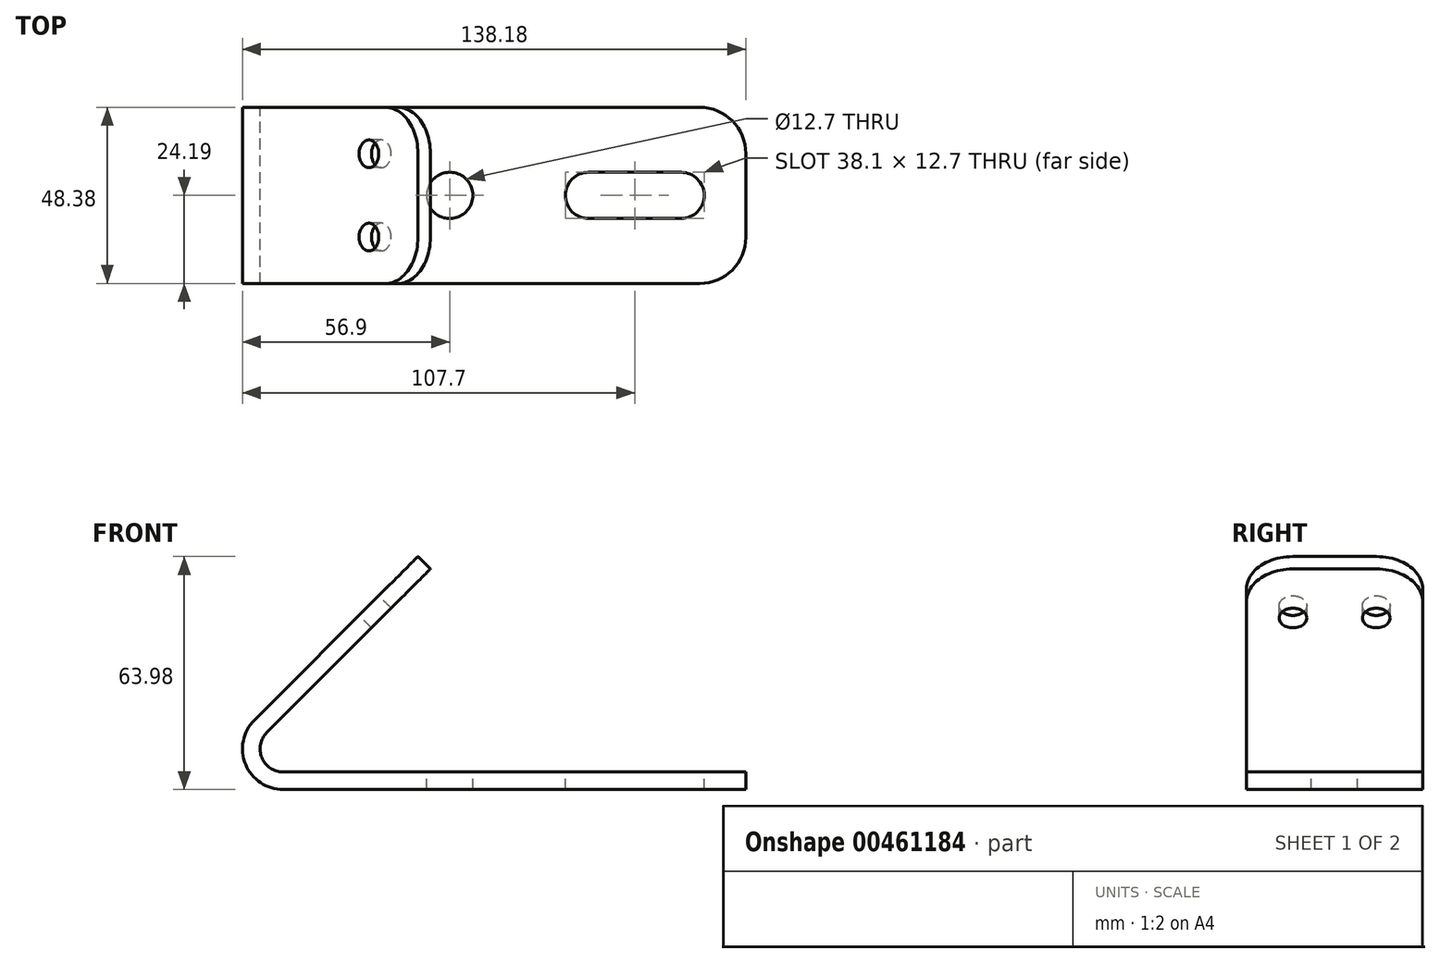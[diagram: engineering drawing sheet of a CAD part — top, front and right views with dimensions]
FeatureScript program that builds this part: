
annotation { "Feature Type Name" : "Feature", "Feature Type Description" : "" }
export const myFeature = defineFeature(function(context is Context, id is Id, definition is map)
    precondition{}
    {
        {
            var Q0;
            Q0=qCreatedBy(makeId("Front.planeOp"),FACE);
            var sketch = newSketch(context, id + "F0", { "sketchPlane" : qUnion([Q0])});
            skLineSegment(sketch, "E0", {"start": v(-8.72, 63.98) * mm, "end": v(-53.62, 19.08) * mm});
            skLineSegment(sketch, "E1", {"start": v(-45.72, 0) * mm, "end": v(81.28, 0) * mm});
            skLineSegment(sketch, "E2", {"start": v(81.28, 0) * mm, "end": v(81.28, 4.83) * mm});
            skLineSegment(sketch, "E3", {"start": v(81.28, 4.83) * mm, "end": v(-45.72, 4.83) * mm});
            skLineSegment(sketch, "E4", {"start": v(-5.3, 60.57) * mm, "end": v(-8.72, 63.98) * mm});
            skPoint(sketch, "E5.visualSharp", {"position": v(-72.7, 0) * mm});
            skArc(sketch, "E5.filletArc", {"start": v(-53.62, 19.08) * mm, "mid": v(-56.05, 6.9) * mm, "end": v(-45.72, 0) * mm});
            skArc(sketch, "E6", {"start": v(-50.21, 15.67) * mm, "mid": v(-51.59, 8.75) * mm, "end": v(-45.72, 4.83) * mm});
            skLineSegment(sketch, "E7.trimOffspring", {"start": v(-50.21, 15.67) * mm, "end": v(-5.3, 60.57) * mm});
            skSolve(sketch);
        }
        {
            var Q0;
            Q0 = qSketchRegion(id + "F0", true);
            extrude(context, id + "F1", {"entities" : qUnion([Q0]), "endBound" : BoundingType.SYMMETRIC, "depth" : 48.4 * mm});
        }
        {
            var Q0;
            Q0=makeQuery(id+"F1.opExtrude","SWEPT_FACE",FACE,{"disambiguationData":[OSD([sQuery(id+"F0.wireOp",EDGE,"E0")])]});
            var sketch = newSketch(context, id + "F2", { "sketchPlane" : qUnion([Q0])});
            skCircle(sketch, "E8", {"center": v(-11.43, 20.02) * mm, "radius": 3.81 * mm});
            skCircle(sketch, "E9", {"center": v(11.43, 20.02) * mm, "radius": 3.81 * mm});
            skSolve(sketch);
        }
        {
            var Q0;
            Q0 = qSketchRegion(id + "F2", true);
            var Q1;
            Q1=makeQuery(id+"F1.opExtrude","SWEPT_FACE",FACE,{"disambiguationData":[OSD([sQuery(id+"F0.wireOp",EDGE,"E7.trimOffspring")])]});
            extrude(context, id + "F3", {"entities" : qUnion([Q0]), "operationType" : NewBodyOperationType.REMOVE, "endBound" : BoundingType.UP_TO_SURFACE, "oppositeDirection" : true, "endBoundEntityFace" : qUnion([Q1]), "depth" : 25.4 * mm});
        }
        {
            var Q0;
            Q0=makeQuery(id+"F1.opExtrude","SWEPT_FACE",FACE,{"disambiguationData":[OSD([sQuery(id+"F0.wireOp",EDGE,"E3")])]});
            var sketch = newSketch(context, id + "F4", { "sketchPlane" : qUnion([Q0])});
            skCircle(sketch, "E10", {"center": v(0, 0) * mm, "radius": 6.35 * mm});
            skArc(sketch, "E11", {"start": v(38.1, 6.35) * mm, "mid": v(31.75, 0) * mm, "end": v(38.1, -6.35) * mm});
            skArc(sketch, "E12", {"start": v(63.5, -6.35) * mm, "mid": v(69.85, 0) * mm, "end": v(63.5, 6.35) * mm});
            skLineSegment(sketch, "E13", {"start": v(38.1, -6.35) * mm, "end": v(63.5, -6.35) * mm});
            skLineSegment(sketch, "E14", {"start": v(63.5, 6.35) * mm, "end": v(38.1, 6.35) * mm});
            skSolve(sketch);
        }
        {
            var Q0;
            Q0 = qSketchRegion(id + "F4", true);
            extrude(context, id + "F5", {"entities" : qUnion([Q0]), "operationType" : NewBodyOperationType.REMOVE, "endBound" : BoundingType.UP_TO_NEXT, "oppositeDirection" : true, "depth" : 25.4 * mm});
        }
        {
            var Q0;
            Q0=makeQuery(id+"F1.opExtrude","CAP_EDGE",EDGE,{"disambiguationData":[OSD([sQuery(id+"F0.wireOp",EDGE,"E4")])],"isStart":false});
            var Q1;
            Q1=makeQuery(id+"F1.opExtrude","CAP_EDGE",EDGE,{"disambiguationData":[OSD([sQuery(id+"F0.wireOp",EDGE,"E4")])],"isStart":true});
            var Q2;
            Q2=makeQuery(id+"F1.opExtrude","CAP_EDGE",EDGE,{"disambiguationData":[OSD([sQuery(id+"F0.wireOp",EDGE,"E2")])],"isStart":true});
            var Q3;
            Q3=makeQuery(id+"F1.opExtrude","CAP_EDGE",EDGE,{"disambiguationData":[OSD([sQuery(id+"F0.wireOp",EDGE,"E2")])],"isStart":false});
            fillet(context, id + "F6", {"entities" : qUnion([Q0, Q1, Q2, Q3]), "radius" : 12.7 * mm, "tangentPropagation" : true, "allowEdgeOverflow" : false});
        }
    });
